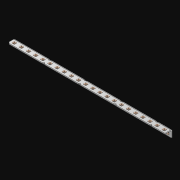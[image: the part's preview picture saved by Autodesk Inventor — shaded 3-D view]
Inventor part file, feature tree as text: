
AUTODESK INVENTOR PART (.ipt)
format: ipt  version: 2021 (Build 250183000, 183)  size: 743,936 bytes
history: native  units: in
note: dims shown in document units (in); Inventor stores cm internally (conversion verified against a paired STEP export)
features: extrude x45, other x44, sketch x3, pattern_linear x1, sheet_metal_op x1
ambient origin geometry x8: Origin, YZ Plane, XZ Plane, XY Plane, X Axis, Y Axis, Z Axis, Center Point
bodies: Solid1 (feature_tree)
feature tree (94):
  pattern_linear  "Rectangular Pattern1"  Spacing1=0.063in  [1 undecoded]
  extrude  "Extrusion1"  Depth=0.5in
  sketch  "Sketch1"  dims[d0=0.182in]
  other  "Srf1"
  sketch  "Sketch2"  dims[d1=0.063in d2=0.0in]
  other  "Srf2"
  other  "Srf3"
  other  "Srf5"
  other  "Srf7"
  other  "Srf9"
  other  "Srf11"
  other  "Srf13"
  other  "Srf15"
  other  "Srf17"
  other  "Srf19"
  other  "Srf21"
  other  "Srf23"
  other  "Srf25"
  other  "Srf27"
  other  "Srf29"
  other  "Srf31"
  other  "Srf33"
  other  "Srf35"
  other  "Srf37"
  other  "Srf39"
  other  "Srf41"
  other  "Srf43"
  other  "Srf4"
  other  "Srf6"
  other  "Srf8"
  other  "Srf10"
  other  "Srf12"
  other  "Srf14"
  other  "Srf16"
  other  "Srf18"
  other  "Srf20"
  other  "Srf22"
  other  "Srf24"
  other  "Srf26"
  other  "Srf28"
  other  "Srf30"
  other  "Srf32"
  other  "Srf34"
  other  "Srf36"
  other  "Srf38"
  other  "Srf40"
  other  "Srf42"
  other  "Srf44"
  sketch  "Sketch3"  dims[d3=0.182in d4=0.063in d5=0.0in d8=0.5in d9=6.5in d10=0.0in]
  sheet_metal_op  "Fold1"
  extrude  "ExtrusionSrf1"  Depth=6.5in TaperAngle=0.0deg
  extrude  "ExtrusionSrf2"  [1 undecoded]
  extrude  "ExtrusionSrf3"  [1 undecoded]
  extrude  "ExtrusionSrf4"  [1 undecoded]
  extrude  "ExtrusionSrf5"  [1 undecoded]
  extrude  "ExtrusionSrf6"  [1 undecoded]
  extrude  "ExtrusionSrf7"  [1 undecoded]
  extrude  "ExtrusionSrf8"  [1 undecoded]
  extrude  "ExtrusionSrf9"  [1 undecoded]
  extrude  "ExtrusionSrf10"  [1 undecoded]
  extrude  "ExtrusionSrf11"  [1 undecoded]
  extrude  "ExtrusionSrf12"  [1 undecoded]
  extrude  "ExtrusionSrf13"  [1 undecoded]
  extrude  "ExtrusionSrf14"  [1 undecoded]
  extrude  "ExtrusionSrf15"  [1 undecoded]
  extrude  "ExtrusionSrf16"  [1 undecoded]
  extrude  "ExtrusionSrf17"  [1 undecoded]
  extrude  "ExtrusionSrf18"  [1 undecoded]
  extrude  "ExtrusionSrf19"  [1 undecoded]
  extrude  "ExtrusionSrf20"  [1 undecoded]
  extrude  "ExtrusionSrf21"  [1 undecoded]
  extrude  "ExtrusionSrf22"  [1 undecoded]
  extrude  "ExtrusionSrf23"  [1 undecoded]
  extrude  "ExtrusionSrf37"  [1 undecoded]
  extrude  "ExtrusionSrf38"  [1 undecoded]
  extrude  "ExtrusionSrf39"  [1 undecoded]
  extrude  "ExtrusionSrf40"  [1 undecoded]
  extrude  "ExtrusionSrf41"  [1 undecoded]
  extrude  "ExtrusionSrf42"  [1 undecoded]
  extrude  "ExtrusionSrf43"  [1 undecoded]
  extrude  "ExtrusionSrf44"  [1 undecoded]
  extrude  "ExtrusionSrf45"  [1 undecoded]
  extrude  "ExtrusionSrf46"  [1 undecoded]
  extrude  "ExtrusionSrf47"  [1 undecoded]
  extrude  "ExtrusionSrf48"  [1 undecoded]
  extrude  "ExtrusionSrf49"  [1 undecoded]
  extrude  "ExtrusionSrf50"  [1 undecoded]
  extrude  "ExtrusionSrf51"  [1 undecoded]
  extrude  "ExtrusionSrf52"  [1 undecoded]
  extrude  "ExtrusionSrf53"  [1 undecoded]
  extrude  "ExtrusionSrf54"  [1 undecoded]
  extrude  "ExtrusionSrf55"  [1 undecoded]
  extrude  "ExtrusionSrf56"  [1 undecoded]
  extrude  "ExtrusionSrf57"  [1 undecoded]
note: 44 required parameter values undecoded (feature->parameter linkage not recoverable at this tier; creation-order binding heuristic only, values carry confidence <= 0.55)
